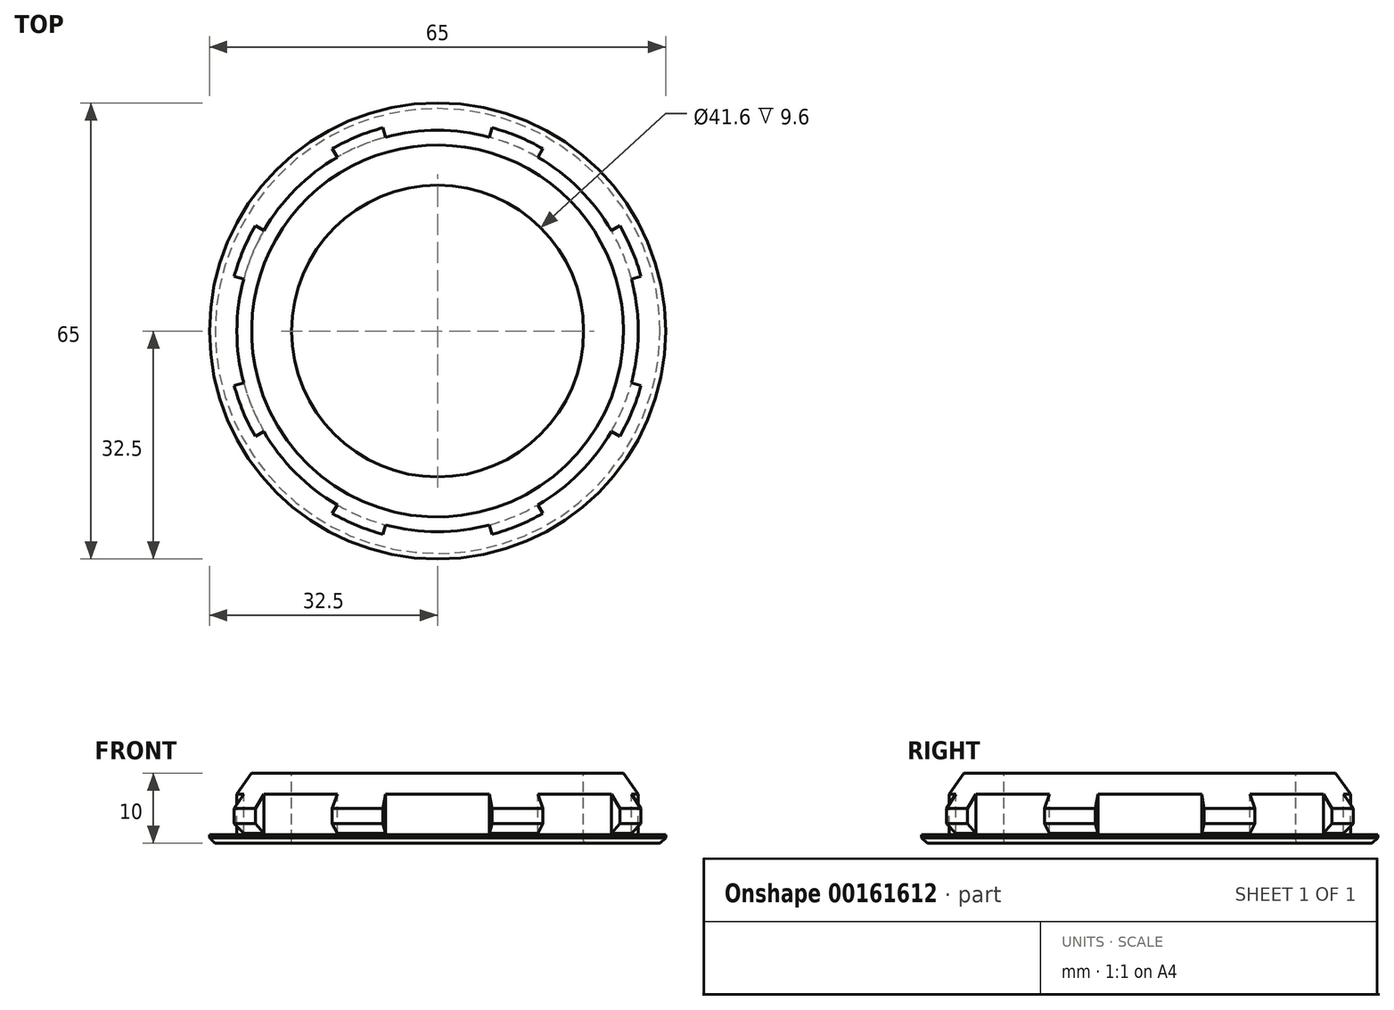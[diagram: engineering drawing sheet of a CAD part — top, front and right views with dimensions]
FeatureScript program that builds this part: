
annotation { "Feature Type Name" : "Feature", "Feature Type Description" : "" }
export const myFeature = defineFeature(function(context is Context, id is Id, definition is map)
    precondition{}
    {
        {
            var Q0;
            Q0=qCreatedBy(makeId("Front.planeOp"),FACE);
            var sketch = newSketch(context, id + "F0", { "sketchPlane" : qUnion([Q0])});
            skLineSegment(sketch, "E0", {"start": v(-32.5, 1.2) * mm, "end": v(-32.5, 0) * mm});
            skLineSegment(sketch, "E1", {"start": v(-32.5, 0) * mm, "end": v(-20.8, 0) * mm});
            skLineSegment(sketch, "E2", {"start": v(-32.5, 1.2) * mm, "end": v(-28.6, 1.2) * mm});
            skLineSegment(sketch, "E3", {"start": v(-28.6, 1.2) * mm, "end": v(-28.6, 1.4) * mm});
            skLineSegment(sketch, "E4", {"start": v(-30, 5) * mm, "end": v(-26.5, 10) * mm});
            skLineSegment(sketch, "E5", {"start": v(-26.5, 10) * mm, "end": v(-20.8, 10) * mm});
            skLineSegment(sketch, "E6", {"start": v(-20.8, 10) * mm, "end": v(-20.8, 0) * mm});
            skLineSegment(sketch, "E7", {"start": v(-20.8, 10) * mm, "end": v(0, 10) * mm, "construction": true});
            skLineSegment(sketch, "E8", {"start": v(0, 10) * mm, "end": v(0, 0) * mm, "construction": true});
            skLineSegment(sketch, "E9", {"start": v(0, 0) * mm, "end": v(-20.8, 0) * mm, "construction": true});
            skLineSegment(sketch, "E10", {"start": v(-30, 2.8) * mm, "end": v(-28.6, 1.4) * mm});
            skLineSegment(sketch, "E11", {"start": v(-30, 5) * mm, "end": v(-30, 2.8) * mm});
            skSolve(sketch);
        }
        {
            var Q0;
            Q0 = qSketchRegion(id + "F0", true);
            var Q1;
            Q1=sQuery(id+"F0.wireOp",EDGE,"E8");
            revolve(context, id + "F1", {"entities" : qUnion([Q0]), "axis" : qUnion([Q1]), "revolveType" : RevolveType.FULL});
        }
        {
            var Q0;
            Q0=qCreatedBy(makeId("Front.planeOp"),FACE);
            var sketch = newSketch(context, id + "F2", { "sketchPlane" : qUnion([Q0])});
            skLineSegment(sketch, "E12", {"start": v(-28.6, 1.2) * mm, "end": v(-28.6, 10) * mm});
            skLineSegment(sketch, "E13", {"start": v(-28.6, 10) * mm, "end": v(0, 10) * mm});
            skLineSegment(sketch, "E14", {"start": v(0, 10) * mm, "end": v(0, 16) * mm});
            skLineSegment(sketch, "E15", {"start": v(0, 16) * mm, "end": v(-31, 16) * mm});
            skLineSegment(sketch, "E16", {"start": v(-31, 16) * mm, "end": v(-31, 1.2) * mm});
            skLineSegment(sketch, "E17", {"start": v(-31, 1.2) * mm, "end": v(-28.6, 1.2) * mm});
            skSolve(sketch);
        }
        {
            var Q0;
            Q0 = qSketchRegion(id + "F2", true);
            var Q1;
            Q1=sQuery(id+"F2.wireOp",EDGE,"E14");
            revolve(context, id + "F3", {"entities" : qUnion([Q0]), "axis" : qUnion([Q1]), "revolveType" : RevolveType.SYMMETRIC, "angle" : 30 * degree});
        }
        {
            var Q0;
            Q0=makeQuery(id+"F3.opRevolve","SWEPT_BODY",BODY,{"disambiguationData":[OSD([sQuery(id+"F2.wireOp",EDGE,"E12"),sQuery(id+"F2.wireOp",EDGE,"E13"),sQuery(id+"F2.wireOp",EDGE,"E14"),sQuery(id+"F2.wireOp",EDGE,"E15"),sQuery(id+"F2.wireOp",EDGE,"E16"),sQuery(id+"F2.wireOp",EDGE,"E17")])]});
            var Q1;
            Q1=makeQuery(id+"F3.opRevolve","CAP_EDGE",EDGE,{"disambiguationData":[OSD([sQuery(id+"F2.wireOp",EDGE,"E14")])],"isStart":true});
            circularPattern(context, id + "F4", {"entities" : qUnion([Q0]), "axis" : qUnion([Q1]), "angle" : 360 * degree, "instanceCount" : 8, "equalSpace" : true});
        }
        {
            var Q0;
            Q0=makeQuery(id+"F4.opPattern","COPY",BODY,{"derivedFrom":makeQuery(id+"F3.opRevolve","SWEPT_BODY",BODY,{"disambiguationData":[OSD([sQuery(id+"F2.wireOp",EDGE,"E12"),sQuery(id+"F2.wireOp",EDGE,"E13"),sQuery(id+"F2.wireOp",EDGE,"E14"),sQuery(id+"F2.wireOp",EDGE,"E15"),sQuery(id+"F2.wireOp",EDGE,"E16"),sQuery(id+"F2.wireOp",EDGE,"E17")])]}),"instanceName":"7"});
            var Q1;
            Q1=makeQuery(id+"F4.opPattern","COPY",BODY,{"derivedFrom":makeQuery(id+"F3.opRevolve","SWEPT_BODY",BODY,{"disambiguationData":[OSD([sQuery(id+"F2.wireOp",EDGE,"E12"),sQuery(id+"F2.wireOp",EDGE,"E13"),sQuery(id+"F2.wireOp",EDGE,"E14"),sQuery(id+"F2.wireOp",EDGE,"E15"),sQuery(id+"F2.wireOp",EDGE,"E16"),sQuery(id+"F2.wireOp",EDGE,"E17")])]}),"instanceName":"6"});
            var Q2;
            Q2=makeQuery(id+"F4.opPattern","COPY",BODY,{"derivedFrom":makeQuery(id+"F3.opRevolve","SWEPT_BODY",BODY,{"disambiguationData":[OSD([sQuery(id+"F2.wireOp",EDGE,"E12"),sQuery(id+"F2.wireOp",EDGE,"E13"),sQuery(id+"F2.wireOp",EDGE,"E14"),sQuery(id+"F2.wireOp",EDGE,"E15"),sQuery(id+"F2.wireOp",EDGE,"E16"),sQuery(id+"F2.wireOp",EDGE,"E17")])]}),"instanceName":"5"});
            var Q3;
            Q3=makeQuery(id+"F4.opPattern","COPY",BODY,{"derivedFrom":makeQuery(id+"F3.opRevolve","SWEPT_BODY",BODY,{"disambiguationData":[OSD([sQuery(id+"F2.wireOp",EDGE,"E12"),sQuery(id+"F2.wireOp",EDGE,"E13"),sQuery(id+"F2.wireOp",EDGE,"E14"),sQuery(id+"F2.wireOp",EDGE,"E15"),sQuery(id+"F2.wireOp",EDGE,"E16"),sQuery(id+"F2.wireOp",EDGE,"E17")])]}),"instanceName":"4"});
            var Q4;
            Q4=makeQuery(id+"F4.opPattern","COPY",BODY,{"derivedFrom":makeQuery(id+"F3.opRevolve","SWEPT_BODY",BODY,{"disambiguationData":[OSD([sQuery(id+"F2.wireOp",EDGE,"E12"),sQuery(id+"F2.wireOp",EDGE,"E13"),sQuery(id+"F2.wireOp",EDGE,"E14"),sQuery(id+"F2.wireOp",EDGE,"E15"),sQuery(id+"F2.wireOp",EDGE,"E16"),sQuery(id+"F2.wireOp",EDGE,"E17")])]}),"instanceName":"3"});
            var Q5;
            Q5=makeQuery(id+"F4.opPattern","COPY",BODY,{"derivedFrom":makeQuery(id+"F3.opRevolve","SWEPT_BODY",BODY,{"disambiguationData":[OSD([sQuery(id+"F2.wireOp",EDGE,"E12"),sQuery(id+"F2.wireOp",EDGE,"E13"),sQuery(id+"F2.wireOp",EDGE,"E14"),sQuery(id+"F2.wireOp",EDGE,"E15"),sQuery(id+"F2.wireOp",EDGE,"E16"),sQuery(id+"F2.wireOp",EDGE,"E17")])]}),"instanceName":"2"});
            var Q6;
            Q6=makeQuery(id+"F4.opPattern","COPY",BODY,{"derivedFrom":makeQuery(id+"F3.opRevolve","SWEPT_BODY",BODY,{"disambiguationData":[OSD([sQuery(id+"F2.wireOp",EDGE,"E12"),sQuery(id+"F2.wireOp",EDGE,"E13"),sQuery(id+"F2.wireOp",EDGE,"E14"),sQuery(id+"F2.wireOp",EDGE,"E15"),sQuery(id+"F2.wireOp",EDGE,"E16"),sQuery(id+"F2.wireOp",EDGE,"E17")])]}),"instanceName":"1"});
            var Q7;
            Q7=makeQuery(id+"F3.opRevolve","SWEPT_BODY",BODY,{"disambiguationData":[OSD([sQuery(id+"F2.wireOp",EDGE,"E12"),sQuery(id+"F2.wireOp",EDGE,"E13"),sQuery(id+"F2.wireOp",EDGE,"E14"),sQuery(id+"F2.wireOp",EDGE,"E15"),sQuery(id+"F2.wireOp",EDGE,"E16"),sQuery(id+"F2.wireOp",EDGE,"E17")])]});
            var Q8;
            Q8=makeQuery(id+"F1.opRevolve","SWEPT_BODY",BODY,{"disambiguationData":[OSD([sQuery(id+"F0.wireOp",EDGE,"E0"),sQuery(id+"F0.wireOp",EDGE,"E1"),sQuery(id+"F0.wireOp",EDGE,"E2"),sQuery(id+"F0.wireOp",EDGE,"E3"),sQuery(id+"F0.wireOp",EDGE,"E4"),sQuery(id+"F0.wireOp",EDGE,"3N1fRAVv-PpJM-oQpf-whvB-sj1A45jDuhM4"),sQuery(id+"F0.wireOp",EDGE,"r6GXPBkd-Ub3N-YDSZ-c9t6-loZOIcQxa3wt"),sQuery(id+"F0.wireOp",EDGE,"E5"),sQuery(id+"F0.wireOp",EDGE,"E6"),sQuery(id+"F0.wireOp",EDGE,"E10"),sQuery(id+"F0.wireOp",EDGE,"E11")])]});
            booleanBodies(context, id + "F5", {"operationType" : BooleanOperationType.SUBTRACTION, "tools" : qUnion([Q0, Q1, Q2, Q3, Q4, Q5, Q6, Q7]), "targets" : qUnion([Q8])});
        }
        {
            var Q0;
            Q0=makeQuery(id+"F1.opRevolve","SWEPT_EDGE",EDGE,{"disambiguationData":[OSD([sQuery(id+"F0.wireOp",EDGE,"E1"),sQuery(id+"F0.wireOp",EDGE,"E6")])]});
            fillet(context, id + "F6", {"entities" : qUnion([Q0]), "radius" : 0.4 * mm, "tangentPropagation" : true, "allowEdgeOverflow" : false});
        }
        {
            var Q0;
            Q0=makeQuery(id+"F1.opRevolve","SWEPT_EDGE",EDGE,{"disambiguationData":[OSD([sQuery(id+"F0.wireOp",EDGE,"E0"),sQuery(id+"F0.wireOp",EDGE,"E1")])]});
            chamfer(context, id + "F7", {"entities" : qUnion([Q0]), "width" : 0.8 * mm, "tangentPropagation" : true});
        }
    });
